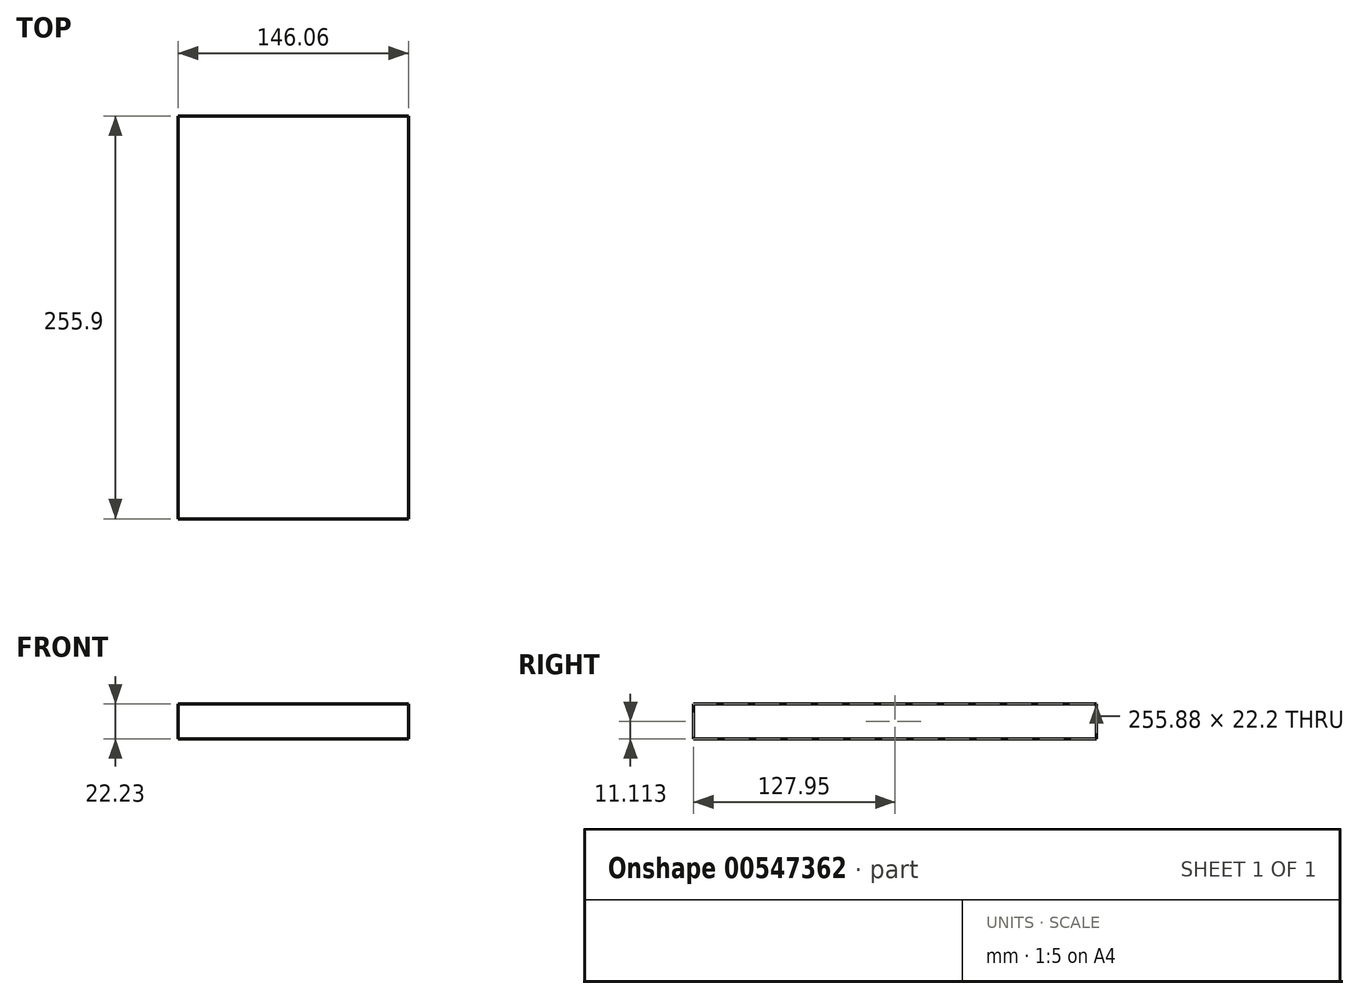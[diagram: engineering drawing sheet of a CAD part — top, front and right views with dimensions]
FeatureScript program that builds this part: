
annotation { "Feature Type Name" : "Feature", "Feature Type Description" : "" }
export const myFeature = defineFeature(function(context is Context, id is Id, definition is map)
    precondition{}
    {
        {
            var Q0;
            Q0=qCreatedBy(makeId("Top.planeOp"),FACE);
            var sketch = newSketch(context, id + "F0", { "sketchPlane" : qUnion([Q0])});
            skLineSegment(sketch, "E0.bottom", {"start": v(73.03, 127.95) * mm, "end": v(-73.03, 127.95) * mm});
            skLineSegment(sketch, "E0.top", {"start": v(73.02, -127.95) * mm, "end": v(-73.03, -127.95) * mm});
            skLineSegment(sketch, "E0.left", {"start": v(73.03, 127.95) * mm, "end": v(73.02, -127.95) * mm});
            skLineSegment(sketch, "E0.right", {"start": v(-73.03, 127.95) * mm, "end": v(-73.03, -127.95) * mm});
            skPoint(sketch, "E0.middle", {"position": v(0, 0) * mm});
            skSolve(sketch);
        }
        {
            var Q0;
            Q0=makeQuery(id+"F0.imprint","IMPRINT",FACE,{"disambiguationData":[TD([[makeQuery(id+"F0.imprint","IMPRINT",EDGE,{"derivedFrom":sQuery(id+"F0.wireOp",EDGE,"E0.bottom")}),1.0]])]});
            extrude(context, id + "F1", {"entities" : qUnion([Q0]), "depth" : 22.22 * mm, "offsetDistance" : 25.4 * mm});
        }
        {
            var Q0;
            Q0=makeQuery(id+"F1.opExtrude","SWEPT_FACE",FACE,{"disambiguationData":[OSD([sQuery(id+"F0.wireOp",EDGE,"E0.right")])]});
            var Q1;
            Q1=makeQuery(id+"F1.opExtrude","SWEPT_FACE",FACE,{"disambiguationData":[OSD([sQuery(id+"F0.wireOp",EDGE,"E0.left")])]});
            shell(context, id + "F2", {"entities" : qUnion([Q0, Q1]), "thickness" : .75 / 50.8 * mm});
        }
    });
